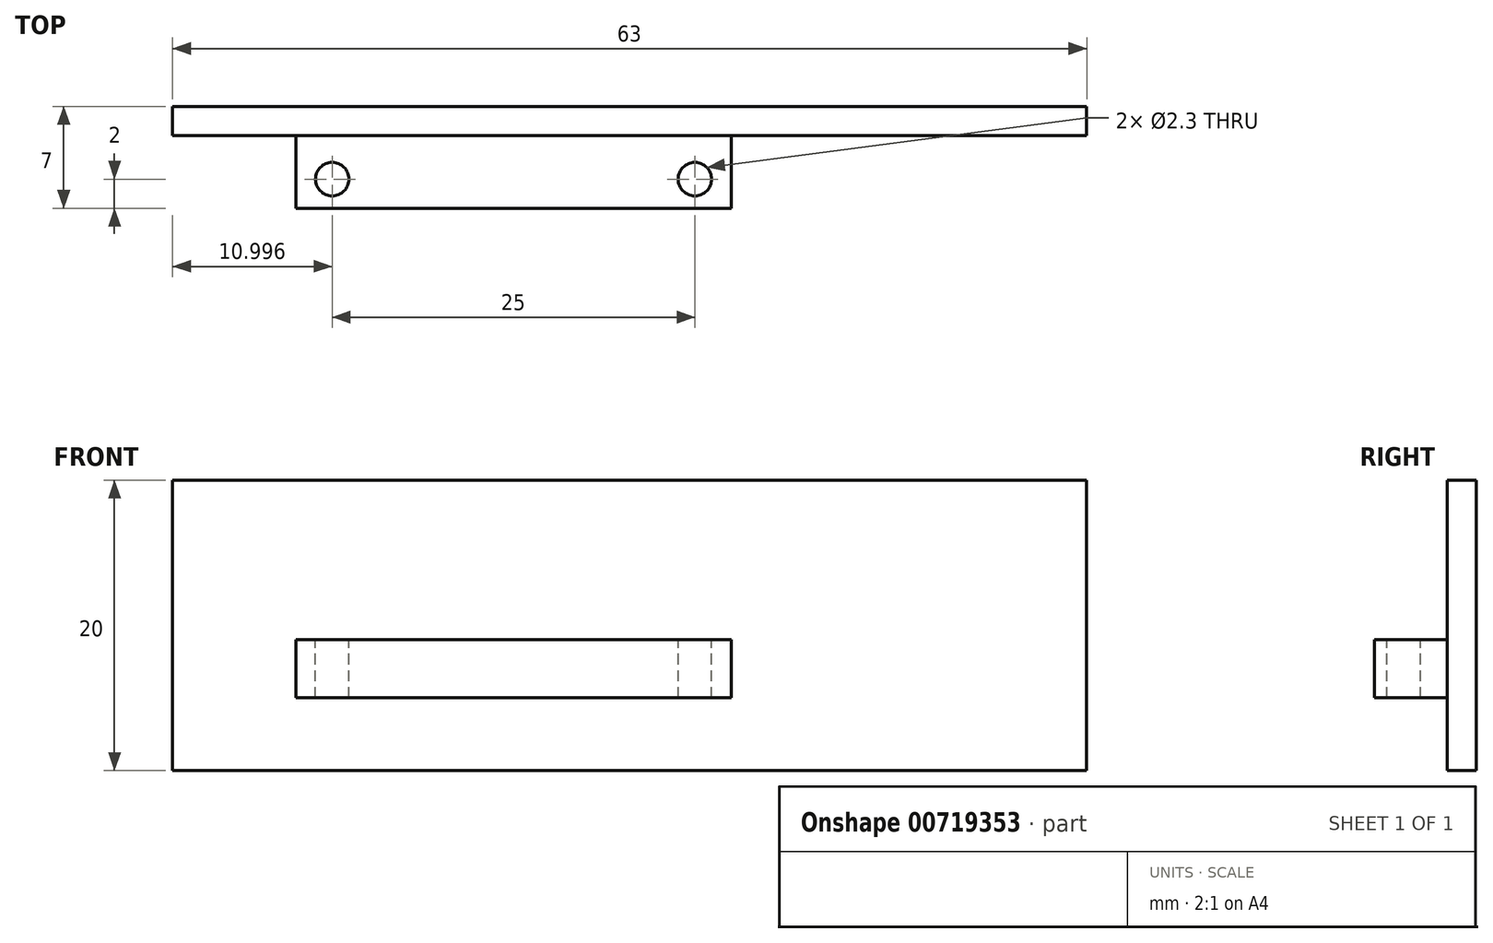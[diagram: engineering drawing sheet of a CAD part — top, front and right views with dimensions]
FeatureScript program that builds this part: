
annotation { "Feature Type Name" : "Feature", "Feature Type Description" : "" }
export const myFeature = defineFeature(function(context is Context, id is Id, definition is map)
    precondition{}
    {
        {
            var Q0;
            Q0=qCreatedBy(makeId("Front.planeOp"),FACE);
            var sketch = newSketch(context, id + "F0", { "sketchPlane" : qUnion([Q0])});
            skLineSegment(sketch, "E0", {"start": v(-32.25, -22.74) * mm, "end": v(-32.25, -32.74) * mm});
            skLineSegment(sketch, "E1", {"start": v(-32.25, -32.74) * mm, "end": v(30.75, -32.74) * mm});
            skLineSegment(sketch, "E2", {"start": v(30.75, -32.74) * mm, "end": v(30.75, -12.74) * mm});
            skLineSegment(sketch, "E3", {"start": v(30.75, -12.74) * mm, "end": v(-32.25, -12.74) * mm});
            skLineSegment(sketch, "E4", {"start": v(-32.25, -12.74) * mm, "end": v(-32.25, -22.74) * mm});
            skSolve(sketch);
        }
        {
            var Q0;
            Q0 = qSketchRegion(id + "F0", true);
            extrude(context, id + "F1", {"entities" : qUnion([Q0]), "depth" : 2 * mm, "offsetDistance" : 25 * mm});
        }
        {
            var Q0;
            Q0=makeQuery(id+"F1.opExtrude","CAP_FACE",FACE,{"disambiguationData":[OSD([sQuery(id+"F0.wireOp",EDGE,"E0"),sQuery(id+"F0.wireOp",EDGE,"E1"),sQuery(id+"F0.wireOp",EDGE,"E2"),sQuery(id+"F0.wireOp",EDGE,"E3"),sQuery(id+"F0.wireOp",EDGE,"E4")])],"isStart":false});
            var sketch = newSketch(context, id + "F2", { "sketchPlane" : qUnion([Q0])});
            skLineSegment(sketch, "E5.bottom", {"start": v(-23.75, -23.74) * mm, "end": v(6.25, -23.74) * mm});
            skLineSegment(sketch, "E5.top", {"start": v(-23.75, -27.74) * mm, "end": v(6.25, -27.74) * mm});
            skLineSegment(sketch, "E5.left", {"start": v(-23.75, -23.74) * mm, "end": v(-23.75, -27.74) * mm});
            skLineSegment(sketch, "E5.right", {"start": v(6.25, -23.74) * mm, "end": v(6.25, -27.74) * mm});
            skSolve(sketch);
        }
        {
            var Q0;
            Q0 = qSketchRegion(id + "F2", true);
            extrude(context, id + "F3", {"entities" : qUnion([Q0]), "operationType" : NewBodyOperationType.ADD, "depth" : 5 * mm, "offsetDistance" : 25 * mm});
        }
        {
            var Q0;
            Q0=makeQuery(id+"F3.opExtrude","SWEPT_FACE",FACE,{"disambiguationData":[OSD([sQuery(id+"F2.wireOp",EDGE,"E5.bottom")])]});
            var sketch = newSketch(context, id + "F4", { "sketchPlane" : qUnion([Q0])});
            skCircle(sketch, "E6", {"center": v(-21.25, -5) * mm, "radius": 1.15 * mm});
            skCircle(sketch, "E7", {"center": v(3.75, -5) * mm, "radius": 1.15 * mm});
            skSolve(sketch);
        }
        {
            var Q0;
            Q0 = qSketchRegion(id + "F4", true);
            extrude(context, id + "F5", {"entities" : qUnion([Q0]), "operationType" : NewBodyOperationType.REMOVE, "oppositeDirection" : true, "depth" : 25 * mm, "offsetDistance" : 25 * mm});
        }
    });
